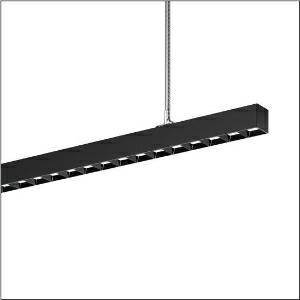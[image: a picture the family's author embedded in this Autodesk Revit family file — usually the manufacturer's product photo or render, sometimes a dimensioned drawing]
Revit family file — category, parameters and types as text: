
# Revit family: silica_21_51mx34dc3dbb
name_source: partatom
category: Lighting Fixtures
units: mm (PartAtom-declared; Revit-internal decimal feet)

## family parameters
Cut with Voids When Loaded = No
Host = Face
Light Source = No
Part Type = Normal
Room Calculation Point = No
Round Connector Dimension = Use Diameter
Shared = No

## types (1)
- --- (1 x LED, 19200 lm, 129.1 W, 3000K)
    Apparent Load = 129 VA
    CIE Flux Codes = 74 94 99 56 100
    Color Rendering = 80
    Color Temperature = 3000K
    Default Elevation = 1800 mm
    Description = Silica 21, office luminaire, primary light control with darklight reflector, of PMMA, black, light emission: direct/indirect distribution, primary light characteristic: asymmetric, installation type: suspended mounting, LED, rated luminous flux: 19.200lm, luminous efficacy: 149lm/W, light colour: 830, colour temperature: 3000K, control gear: DALI 2, with terminal, 3+2-pole, max. 2.5mm², mains connection: 220..240V, AC, 50/60Hz, rated input power: 129.1W, luminaire housing, of aluminium, matt jet black (RAL 9005), length: 3.004mm, width: 53mm, height: 53mm, protection rating (complete): IP20, insulation class (complete): insulation class I (protective earthing), certification: CE, permissible operating ambient temperature: 0..+35°C, standard: EN 50419, packaging unit: 1 piece
    Height = 53 mm
    Lamp = 1 x LED
    Lamp Light Flux = 19200 lm
    Lamp Power = 129.1 W
    Lamp count = 1
    Length = 3004 mm
    Luminous efficacy = 149 lm/W
    Manufacturer = Siteco
    ModVariant = No
    Model = 51MX34DC3DBB
    Mounting Place = Ceiling
    Mounting Type = Pendant
    Number of Poles = 1
    OnlyDefault = Yes
    Power Factor = 1
    Product Name = Silica 21
    Product group = office luminaire | ceiling pendant
    ProductGroupID = 903
    Protection Class = Protection class I
    Protection Degree = IP 20
    RLX_Detail_Level = 1
    RLX_Emergency_Light_Flux = 0 lm
    RLX_Emergency_Type = 0
    RLX_Emergency_Type_DB = No
    RlxData = <blob elided: 68081 chars, md5=15ee5128>
    Socket = socket
    Standby Power = 0 W
    System Light Flux = 19200 lm
    System Power = 129 W
    Type Comments = factory setting: luminous flux: 100 % | dim-lin: 254 | 448 mA
    Type Image = l_1335852.jpg
    URL = http://relux.com
    VarID = @adj_120219
    Voltage = 0 V
    Weight = 0.00 kg
    Width = 53 mm

## geometry (parser evidence)
native form markers: Blend x4, Sweep x10
no freeform markers — native parametric forms only
